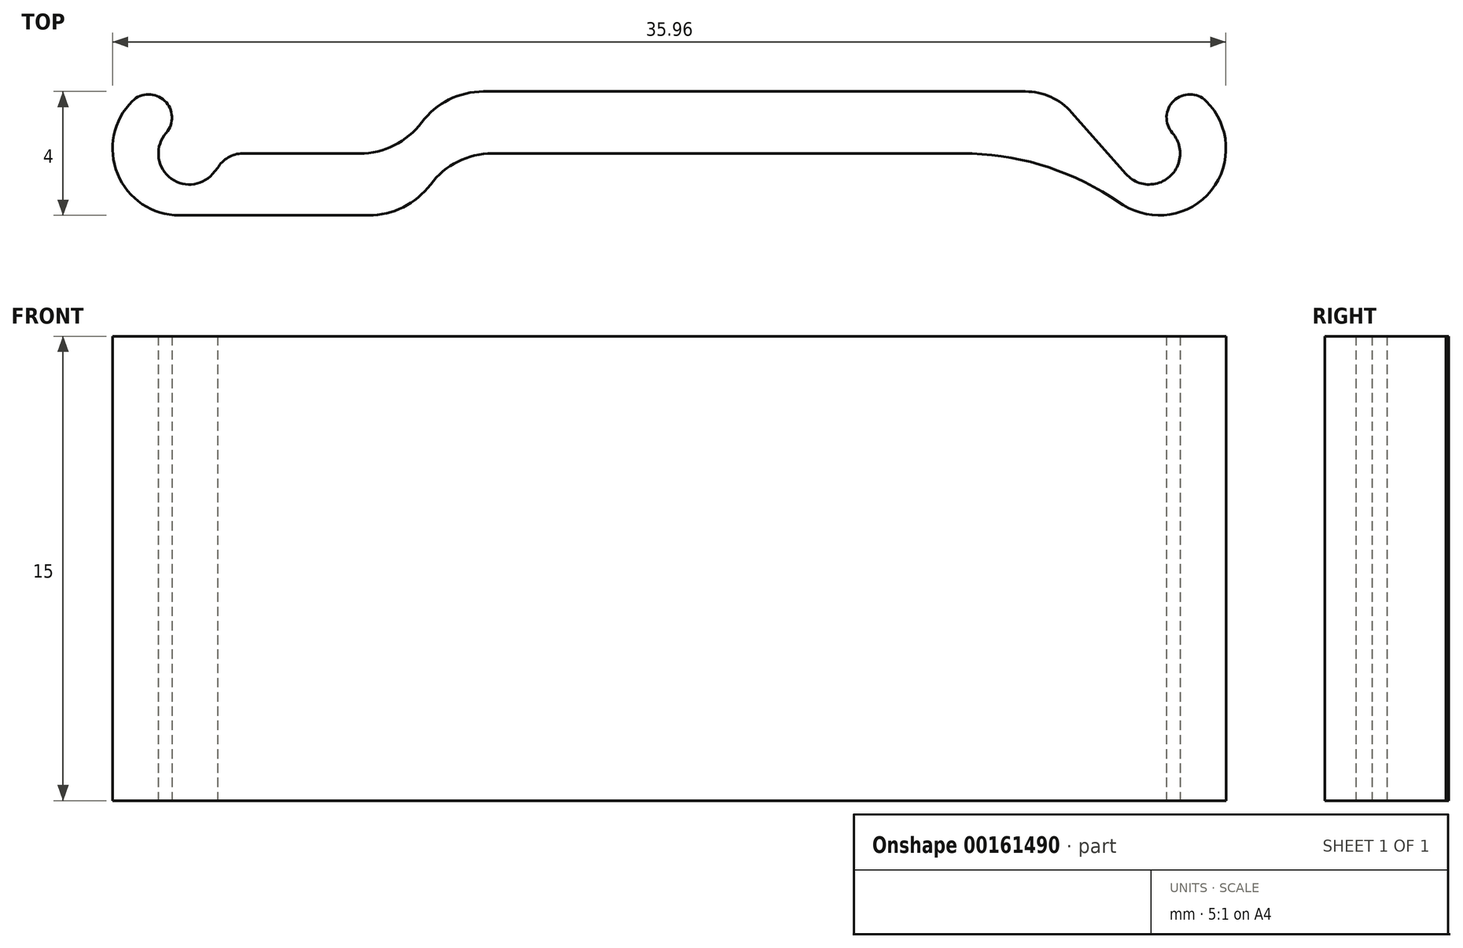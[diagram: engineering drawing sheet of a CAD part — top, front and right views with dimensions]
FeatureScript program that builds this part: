
annotation { "Feature Type Name" : "Feature", "Feature Type Description" : "" }
export const myFeature = defineFeature(function(context is Context, id is Id, definition is map)
    precondition{}
    {
        {
            var Q0;
            Q0=qCreatedBy(makeId("Top.planeOp"),FACE);
            var sketch = newSketch(context, id + "F0", { "sketchPlane" : qUnion([Q0])});
            skLineSegment(sketch, "E0", {"start": v(0, 0) * mm, "end": v(12.4, 0) * mm, "construction": true});
            skLineSegment(sketch, "E1", {"start": v(13.9, -0.68) * mm, "end": v(16.25, -3.34) * mm, "construction": true});
            skArc(sketch, "E2", {"start": v(16.25, -3.34) * mm, "mid": v(16.16, -4.75) * mm, "end": v(14.75, -4.66) * mm, "construction": true});
            skLineSegment(sketch, "E3", {"start": v(14.75, -4.66) * mm, "end": v(13, -2.68) * mm, "construction": true});
            skLineSegment(sketch, "E4", {"start": v(11.5, -2) * mm, "end": v(0, -2) * mm, "construction": true});
            skPoint(sketch, "E5.visualSharp", {"position": v(12.4, -2) * mm});
            skArc(sketch, "E5.filletArc", {"start": v(13, -2.68) * mm, "mid": v(12.32, -2.18) * mm, "end": v(11.5, -2) * mm, "construction": true});
            skPoint(sketch, "E6.visualSharp", {"position": v(13.3, 0) * mm});
            skArc(sketch, "E6.filletArc", {"start": v(13.9, -0.68) * mm, "mid": v(13.23, -0.18) * mm, "end": v(12.4, 0) * mm, "construction": true});
            skLineSegment(sketch, "E7", {"start": v(-6, -2) * mm, "end": v(11.5, -2) * mm});
            skArc(sketch, "E8", {"start": v(11.5, -2) * mm, "mid": v(12.32, -2.18) * mm, "end": v(13, -2.68) * mm});
            skLineSegment(sketch, "E9", {"start": v(13, -2.68) * mm, "end": v(14.75, -4.66) * mm});
            skArc(sketch, "E10", {"start": v(14.75, -4.66) * mm, "mid": v(16.16, -4.75) * mm, "end": v(16.25, -3.34) * mm});
            skArc(sketch, "E11", {"start": v(16.25, -3.34) * mm, "mid": v(16.3, -2.3) * mm, "end": v(17.34, -2.3) * mm});
            skArc(sketch, "E12", {"start": v(17.34, -2.3) * mm, "mid": v(17.51, -5.19) * mm, "end": v(14.66, -5.66) * mm});
            skLineSegment(sketch, "E13", {"start": v(14.66, -5.66) * mm, "end": v(14.25, -5.4) * mm});
            skArc(sketch, "E14", {"start": v(14.25, -5.4) * mm, "mid": v(11.96, -4.36) * mm, "end": v(9.47, -4) * mm});
            skLineSegment(sketch, "E15", {"start": v(9.47, -4) * mm, "end": v(-5.71, -4) * mm});
            skArc(sketch, "E16", {"start": v(-9.71, -6) * mm, "mid": v(-8.6, -5.74) * mm, "end": v(-7.71, -5) * mm});
            skArc(sketch, "E17", {"start": v(-7.71, -5) * mm, "mid": v(-6.83, -4.26) * mm, "end": v(-5.71, -4) * mm});
            skArc(sketch, "E18.MirrorCS", {"start": v(-11.5, -2) * mm, "mid": v(-12.32, -2.18) * mm, "end": v(-13, -2.68) * mm, "construction": true});
            skArc(sketch, "E19.MirrorCS", {"start": v(-16.25, -3.34) * mm, "mid": v(-16.16, -4.75) * mm, "end": v(-14.75, -4.66) * mm, "construction": true});
            skArc(sketch, "E20.MirrorCS", {"start": v(-13.9, -0.68) * mm, "mid": v(-13.23, -0.18) * mm, "end": v(-12.4, 0) * mm, "construction": true});
            skLineSegment(sketch, "E21.MirrorCS", {"start": v(0, 0) * mm, "end": v(-12.4, 0) * mm, "construction": true});
            skLineSegment(sketch, "E22.MirrorCS", {"start": v(-13.9, -0.68) * mm, "end": v(-16.25, -3.34) * mm, "construction": true});
            skPoint(sketch, "E23.MirrorP", {"position": v(-13.3, 0) * mm});
            skArc(sketch, "E24.MirrorCS", {"start": v(-17.34, -2.3) * mm, "mid": v(-17.82, -4.66) * mm, "end": v(-15.82, -6) * mm});
            skArc(sketch, "E25.MirrorCS", {"start": v(-16.25, -3.34) * mm, "mid": v(-16.3, -2.3) * mm, "end": v(-17.34, -2.3) * mm});
            skArc(sketch, "E26.MirrorCS", {"start": v(-14.75, -4.66) * mm, "mid": v(-16.16, -4.75) * mm, "end": v(-16.25, -3.34) * mm});
            skLineSegment(sketch, "E27.MirrorCS", {"start": v(-13, -2.68) * mm, "end": v(-14.75, -4.66) * mm, "construction": true});
            skLineSegment(sketch, "E28", {"start": v(-15.82, -6) * mm, "end": v(-9.71, -6) * mm});
            skLineSegment(sketch, "E29", {"start": v(-13.78, -4) * mm, "end": v(-10, -4) * mm});
            skArc(sketch, "E30", {"start": v(-10, -4) * mm, "mid": v(-8.88, -3.74) * mm, "end": v(-8, -3) * mm});
            skArc(sketch, "E31", {"start": v(-8, -3) * mm, "mid": v(-7.12, -2.26) * mm, "end": v(-6, -2) * mm});
            skArc(sketch, "E32", {"start": v(-13.78, -4) * mm, "mid": v(-14.25, -4.13) * mm, "end": v(-14.59, -4.48) * mm});
            skLineSegment(sketch, "E33", {"start": v(-14.75, -4.66) * mm, "end": v(-14.59, -4.48) * mm});
            skLineSegment(sketch, "E34", {"start": v(-11.5, -2) * mm, "end": v(0, -2) * mm, "construction": true});
            skSolve(sketch);
        }
        {
            var Q0;
            Q0 = qSketchRegion(id + "F0", true);
            extrude(context, id + "F1", {"entities" : qUnion([Q0]), "depth" : 15 * mm});
        }
    });
